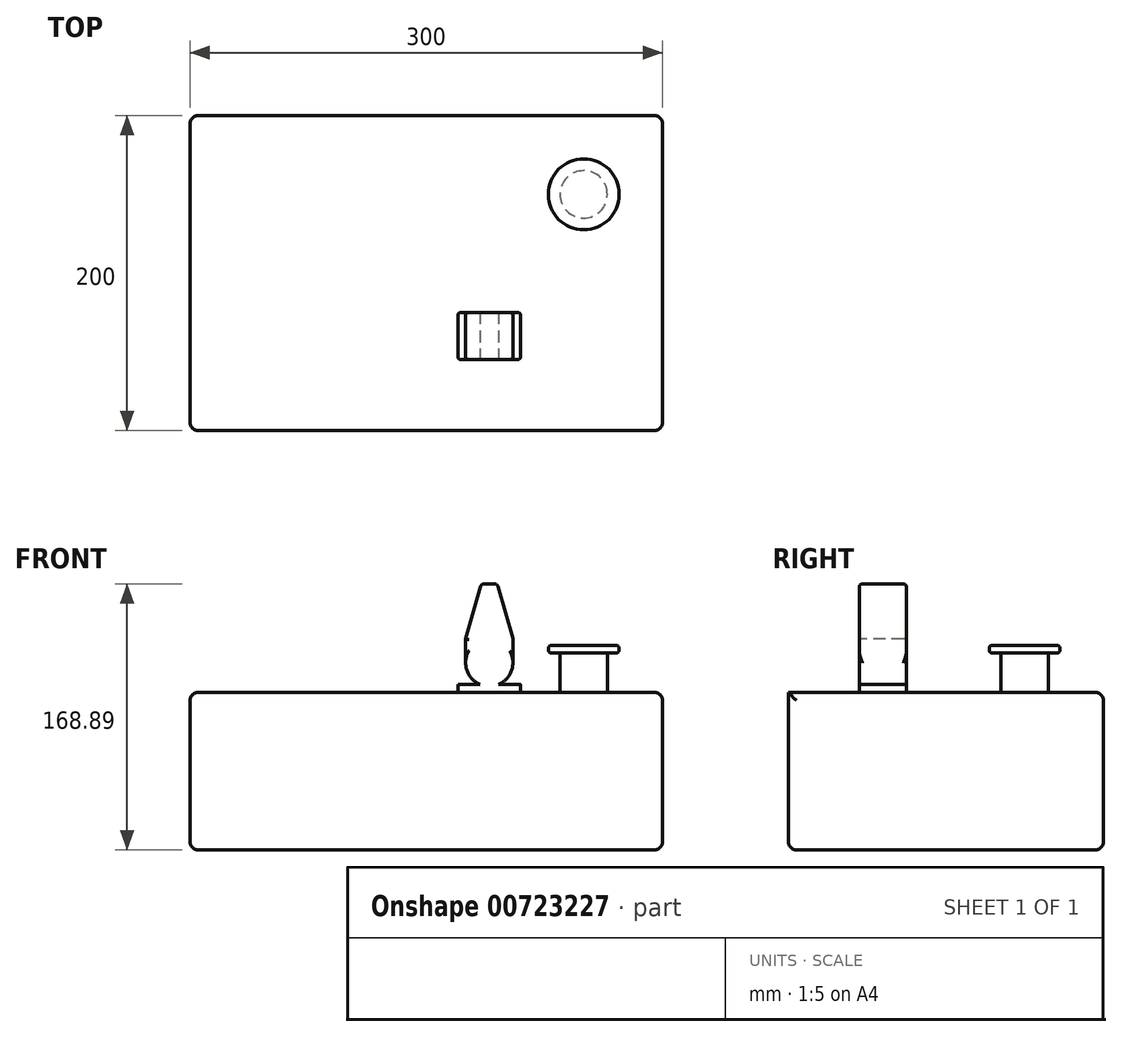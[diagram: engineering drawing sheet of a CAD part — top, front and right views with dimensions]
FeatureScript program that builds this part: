
annotation { "Feature Type Name" : "Feature", "Feature Type Description" : "" }
export const myFeature = defineFeature(function(context is Context, id is Id, definition is map)
    precondition{}
    {
        {
            var Q0;
            Q0=qCreatedBy(makeId("Top.planeOp"),FACE);
            var sketch = newSketch(context, id + "F0", { "sketchPlane" : qUnion([Q0])});
            skLineSegment(sketch, "E0.bottom", {"start": v(-150, 100) * mm, "end": v(150, 100) * mm});
            skLineSegment(sketch, "E0.top", {"start": v(-150, -100) * mm, "end": v(150, -100) * mm});
            skLineSegment(sketch, "E0.left", {"start": v(-150, 100) * mm, "end": v(-150, -100) * mm});
            skLineSegment(sketch, "E0.right", {"start": v(150, 100) * mm, "end": v(150, -100) * mm});
            skSolve(sketch);
        }
        {
            var Q0;
            Q0 = qSketchRegion(id + "F0", true);
            extrude(context, id + "F1", {"entities" : qUnion([Q0]), "depth" : 100 * mm, "offsetDistance" : 25 * mm});
        }
        {
            var Q0;
            Q0=makeQuery(id+"F1.opExtrude","SWEPT_FACE",FACE,{"disambiguationData":[OSD([sQuery(id+"F0.wireOp",EDGE,"E0.top")])]});
            var sketch = newSketch(context, id + "F2", { "sketchPlane" : qUnion([Q0])});
            skLineSegment(sketch, "E1.bottom", {"start": v(20, 100) * mm, "end": v(60, 100) * mm});
            skLineSegment(sketch, "E1.top", {"start": v(20, 105) * mm, "end": v(34.22, 105) * mm});
            skLineSegment(sketch, "E1.left", {"start": v(20, 100) * mm, "end": v(20, 105) * mm});
            skLineSegment(sketch, "E1.right", {"start": v(60, 100) * mm, "end": v(60, 105) * mm});
            skArc(sketch, "E2", {"start": v(25, 118.89) * mm, "mid": v(27.5, 110.54) * mm, "end": v(34.22, 105) * mm});
            skLineSegment(sketch, "E3.top", {"start": v(35, 168.89) * mm, "end": v(45, 168.89) * mm});
            skLineSegment(sketch, "E3.left", {"start": v(25, 118.89) * mm, "end": v(25, 133.89) * mm});
            skLineSegment(sketch, "E3.right", {"start": v(55, 118.89) * mm, "end": v(55, 133.89) * mm});
            skLineSegment(sketch, "E4", {"start": v(35, 168.89) * mm, "end": v(25, 133.89) * mm});
            skLineSegment(sketch, "E5", {"start": v(45, 168.89) * mm, "end": v(55, 133.89) * mm});
            skPoint(sketch, "E6.orphan", {"position": v(25, 168.89) * mm});
            skArc(sketch, "E7.trimOffspring", {"start": v(45.78, 105) * mm, "mid": v(52.5, 110.54) * mm, "end": v(55, 118.89) * mm});
            skLineSegment(sketch, "E8.trimOffspring", {"start": v(45.78, 105) * mm, "end": v(60, 105) * mm});
            skSolve(sketch);
        }
        {
            var Q0;
            Q0 = qSketchRegion(id + "F2", true);
            extrude(context, id + "F3", {"entities" : qUnion([Q0]), "operationType" : NewBodyOperationType.ADD, "oppositeDirection" : true, "depth" : 75 * mm, "offsetDistance" : 25 * mm});
        }
        {
            var Q0;
            Q0=makeQuery(id+"F3.boolean.opBoolean","MERGE",FACE,{"derivedFrom":[makeQuery(id+"F1.opExtrude","SWEPT_FACE",FACE,{"disambiguationData":[OSD([sQuery(id+"F0.wireOp",EDGE,"E0.top")])]}),makeQuery(id+"F3.opExtrude","CAP_FACE",FACE,{"disambiguationData":[OSD([sQuery(id+"F2.wireOp",EDGE,"E1.bottom"),sQuery(id+"F2.wireOp",EDGE,"E1.top"),sQuery(id+"F2.wireOp",EDGE,"E1.left"),sQuery(id+"F2.wireOp",EDGE,"E1.right"),sQuery(id+"F2.wireOp",EDGE,"E2"),sQuery(id+"F2.wireOp",EDGE,"E3.top"),sQuery(id+"F2.wireOp",EDGE,"E3.left"),sQuery(id+"F2.wireOp",EDGE,"E3.right"),sQuery(id+"F2.wireOp",EDGE,"E4"),sQuery(id+"F2.wireOp",EDGE,"E5"),sQuery(id+"F2.wireOp",EDGE,"E7.trimOffspring"),sQuery(id+"F2.wireOp",EDGE,"E8.trimOffspring")])],"isStart":true})]});
            var sketch = newSketch(context, id + "F4", { "sketchPlane" : qUnion([Q0])});
            skLineSegment(sketch, "E9.bottom", {"start": v(9.86, 100) * mm, "end": v(69.53, 100) * mm});
            skLineSegment(sketch, "E9.top", {"start": v(9.86, 173.18) * mm, "end": v(69.53, 173.18) * mm});
            skLineSegment(sketch, "E9.left", {"start": v(9.86, 100) * mm, "end": v(9.86, 173.18) * mm});
            skLineSegment(sketch, "E9.right", {"start": v(69.53, 100) * mm, "end": v(69.53, 173.18) * mm});
            skSolve(sketch);
        }
        {
            var Q0;
            Q0 = qSketchRegion(id + "F4", true);
            extrude(context, id + "F5", {"entities" : qUnion([Q0]), "operationType" : NewBodyOperationType.REMOVE, "oppositeDirection" : true, "depth" : 45 * mm, "offsetDistance" : 25 * mm});
        }
        {
            var Q0;
            Q0=makeQuery(id+"F5.boolean.opBoolean","MERGE",FACE,{"derivedFrom":[makeQuery(id+"F1.opExtrude","CAP_FACE",FACE,{"disambiguationData":[OSD([sQuery(id+"F0.wireOp",EDGE,"E0.bottom"),sQuery(id+"F0.wireOp",EDGE,"E0.top"),sQuery(id+"F0.wireOp",EDGE,"E0.left"),sQuery(id+"F0.wireOp",EDGE,"E0.right")])],"isStart":false}),makeQuery(id+"F5.opExtrude","SWEPT_FACE",FACE,{"disambiguationData":[OSD([sQuery(id+"F4.wireOp",EDGE,"E9.bottom")])]})]});
            var sketch = newSketch(context, id + "F6", { "sketchPlane" : qUnion([Q0])});
            skCircle(sketch, "E10", {"center": v(100, 50) * mm, "radius": 15 * mm});
            skSolve(sketch);
        }
        {
            var Q0;
            Q0 = qSketchRegion(id + "F6", true);
            extrude(context, id + "F7", {"entities" : qUnion([Q0]), "operationType" : NewBodyOperationType.ADD, "depth" : 25 * mm, "offsetDistance" : 25 * mm});
        }
        {
            var Q0;
            Q0=makeQuery(id+"F7.opExtrude","CAP_FACE",FACE,{"disambiguationData":[OSD([sQuery(id+"F6.wireOp",EDGE,"E10")])],"isStart":false});
            var sketch = newSketch(context, id + "F8", { "sketchPlane" : qUnion([Q0])});
            skCircle(sketch, "E11", {"center": v(100, 50) * mm, "radius": 22.5 * mm});
            skSolve(sketch);
        }
        {
            var Q0;
            Q0 = qSketchRegion(id + "F8", true);
            extrude(context, id + "F9", {"entities" : qUnion([Q0]), "operationType" : NewBodyOperationType.ADD, "depth" : 5 * mm, "offsetDistance" : 25 * mm});
        }
        {
            var Q0;
            Q0=makeQuery(id+"F5.boolean.opBoolean","INTERSECT",EDGE,{"derivedFrom":[makeQuery(id+"F3.opExtrude","SWEPT_FACE",FACE,{"disambiguationData":[OSD([sQuery(id+"F2.wireOp",EDGE,"E4")])]}),makeQuery(id+"F5.opExtrude","CAP_FACE",FACE,{"disambiguationData":[OSD([sQuery(id+"F4.wireOp",EDGE,"E9.bottom"),sQuery(id+"F4.wireOp",EDGE,"E9.top"),sQuery(id+"F4.wireOp",EDGE,"E9.left"),sQuery(id+"F4.wireOp",EDGE,"E9.right")])],"isStart":false})]});
            var Q1;
            Q1=makeQuery(id+"F5.boolean.opBoolean","INTERSECT",EDGE,{"derivedFrom":[makeQuery(id+"F3.opExtrude","SWEPT_FACE",FACE,{"disambiguationData":[OSD([sQuery(id+"F2.wireOp",EDGE,"E5")])]}),makeQuery(id+"F5.opExtrude","CAP_FACE",FACE,{"disambiguationData":[OSD([sQuery(id+"F4.wireOp",EDGE,"E9.bottom"),sQuery(id+"F4.wireOp",EDGE,"E9.top"),sQuery(id+"F4.wireOp",EDGE,"E9.left"),sQuery(id+"F4.wireOp",EDGE,"E9.right")])],"isStart":false})]});
            var Q2;
            Q2=makeQuery(id+"F3.opExtrude","SWEPT_EDGE",EDGE,{"disambiguationData":[OSD([sQuery(id+"F2.wireOp",EDGE,"E3.right"),sQuery(id+"F2.wireOp",EDGE,"E5")])]});
            var Q3;
            Q3=makeQuery(id+"F3.opExtrude","CAP_EDGE",EDGE,{"disambiguationData":[OSD([sQuery(id+"F2.wireOp",EDGE,"E4")])],"isStart":false});
            var Q4;
            Q4=makeQuery(id+"F3.opExtrude","CAP_EDGE",EDGE,{"disambiguationData":[OSD([sQuery(id+"F2.wireOp",EDGE,"E3.left")])],"isStart":false});
            var Q5;
            Q5=makeQuery(id+"F3.opExtrude","CAP_EDGE",EDGE,{"disambiguationData":[OSD([sQuery(id+"F2.wireOp",EDGE,"E3.right")])],"isStart":false});
            var Q6;
            Q6=makeQuery(id+"F5.boolean.opBoolean","INTERSECT",EDGE,{"derivedFrom":[makeQuery(id+"F3.opExtrude","SWEPT_FACE",FACE,{"disambiguationData":[OSD([sQuery(id+"F2.wireOp",EDGE,"E3.right")])]}),makeQuery(id+"F5.opExtrude","CAP_FACE",FACE,{"disambiguationData":[OSD([sQuery(id+"F4.wireOp",EDGE,"E9.bottom"),sQuery(id+"F4.wireOp",EDGE,"E9.top"),sQuery(id+"F4.wireOp",EDGE,"E9.left"),sQuery(id+"F4.wireOp",EDGE,"E9.right")])],"isStart":false})]});
            var Q7;
            Q7=makeQuery(id+"F5.boolean.opBoolean","INTERSECT",EDGE,{"derivedFrom":[makeQuery(id+"F3.opExtrude","SWEPT_FACE",FACE,{"disambiguationData":[OSD([sQuery(id+"F2.wireOp",EDGE,"E3.left")])]}),makeQuery(id+"F5.opExtrude","CAP_FACE",FACE,{"disambiguationData":[OSD([sQuery(id+"F4.wireOp",EDGE,"E9.bottom"),sQuery(id+"F4.wireOp",EDGE,"E9.top"),sQuery(id+"F4.wireOp",EDGE,"E9.left"),sQuery(id+"F4.wireOp",EDGE,"E9.right")])],"isStart":false})]});
            var Q8;
            Q8=makeQuery(id+"F3.opExtrude","CAP_EDGE",EDGE,{"disambiguationData":[OSD([sQuery(id+"F2.wireOp",EDGE,"E1.left")])],"isStart":false});
            var Q9;
            Q9=makeQuery(id+"F3.opExtrude","CAP_EDGE",EDGE,{"disambiguationData":[OSD([sQuery(id+"F2.wireOp",EDGE,"E1.right")])],"isStart":false});
            var Q10;
            Q10=makeQuery(id+"F5.boolean.opBoolean","INTERSECT",EDGE,{"derivedFrom":[makeQuery(id+"F3.opExtrude","SWEPT_FACE",FACE,{"disambiguationData":[OSD([sQuery(id+"F2.wireOp",EDGE,"E1.left")])]}),makeQuery(id+"F5.opExtrude","CAP_FACE",FACE,{"disambiguationData":[OSD([sQuery(id+"F4.wireOp",EDGE,"E9.bottom"),sQuery(id+"F4.wireOp",EDGE,"E9.top"),sQuery(id+"F4.wireOp",EDGE,"E9.left"),sQuery(id+"F4.wireOp",EDGE,"E9.right")])],"isStart":false})]});
            var Q11;
            Q11=makeQuery(id+"F5.boolean.opBoolean","INTERSECT",EDGE,{"derivedFrom":[makeQuery(id+"F3.opExtrude","SWEPT_FACE",FACE,{"disambiguationData":[OSD([sQuery(id+"F2.wireOp",EDGE,"E1.right")])]}),makeQuery(id+"F5.opExtrude","CAP_FACE",FACE,{"disambiguationData":[OSD([sQuery(id+"F4.wireOp",EDGE,"E9.bottom"),sQuery(id+"F4.wireOp",EDGE,"E9.top"),sQuery(id+"F4.wireOp",EDGE,"E9.left"),sQuery(id+"F4.wireOp",EDGE,"E9.right")])],"isStart":false})]});
            var Q12;
            Q12=makeQuery(id+"F9.opExtrude","CAP_EDGE",EDGE,{"disambiguationData":[OSD([sQuery(id+"F8.wireOp",EDGE,"E11")])],"isStart":false});
            var Q13;
            Q13=makeQuery(id+"F9.opExtrude","CAP_EDGE",EDGE,{"disambiguationData":[OSD([sQuery(id+"F8.wireOp",EDGE,"E11")])],"isStart":true});
            var Q14;
            Q14=makeQuery(id+"F3.opExtrude","CAP_EDGE",EDGE,{"disambiguationData":[OSD([sQuery(id+"F2.wireOp",EDGE,"E5")])],"isStart":false});
            var Q15;
            Q15=makeQuery(id+"F3.opExtrude","SWEPT_EDGE",EDGE,{"disambiguationData":[OSD([sQuery(id+"F2.wireOp",EDGE,"E3.top"),sQuery(id+"F2.wireOp",EDGE,"E5")])]});
            var Q16;
            Q16=makeQuery(id+"F3.opExtrude","SWEPT_EDGE",EDGE,{"disambiguationData":[OSD([sQuery(id+"F2.wireOp",EDGE,"E3.top"),sQuery(id+"F2.wireOp",EDGE,"E4")])]});
            var Q17;
            Q17=makeQuery(id+"F3.opExtrude","CAP_EDGE",EDGE,{"disambiguationData":[OSD([sQuery(id+"F2.wireOp",EDGE,"E3.top")])],"isStart":false});
            var Q18;
            Q18=makeQuery(id+"F5.boolean.opBoolean","INTERSECT",EDGE,{"derivedFrom":[makeQuery(id+"F3.opExtrude","SWEPT_FACE",FACE,{"disambiguationData":[OSD([sQuery(id+"F2.wireOp",EDGE,"E3.top")])]}),makeQuery(id+"F5.opExtrude","CAP_FACE",FACE,{"disambiguationData":[OSD([sQuery(id+"F4.wireOp",EDGE,"E9.bottom"),sQuery(id+"F4.wireOp",EDGE,"E9.top"),sQuery(id+"F4.wireOp",EDGE,"E9.left"),sQuery(id+"F4.wireOp",EDGE,"E9.right")])],"isStart":false})]});
            fillet(context, id + "F10", {"entities" : qUnion([Q0, Q1, Q2, Q3, Q4, Q5, Q6, Q7, Q8, Q9, Q10, Q11, Q12, Q13, Q14, Q15, Q16, Q17, Q18]), "radius" : 2 * mm, "tangentPropagation" : true, "allowEdgeOverflow" : false});
        }
        {
            var Q0;
            {var subQ3=sQuery(id+"F0.wireOp",EDGE,"E0.right");var subQ4=sQuery(id+"F0.wireOp",EDGE,"E0.top");var subQ6=sQuery(id+"F0.wireOp",EDGE,"E0.left");var subQ8=makeQuery(id+"F1.opExtrude","CAP_EDGE",EDGE,{"disambiguationData":[OSD([subQ4])],"isStart":false});Q0=makeQuery(id+"F5.boolean.opBoolean","MERGE",EDGE,{"derivedFrom":[makeQuery(id+"F3.boolean.opBoolean","SPLIT",EDGE,{"disambiguationData":[TD([makeQuery(id+"F1.opExtrude","SWEPT_FACE",FACE,{"disambiguationData":[OSD([subQ6])]})])],"derivedFrom":subQ8}),makeQuery(id+"F3.boolean.opBoolean","SPLIT",EDGE,{"disambiguationData":[TD([makeQuery(id+"F1.opExtrude","SWEPT_FACE",FACE,{"disambiguationData":[OSD([subQ3])]})])],"derivedFrom":subQ8}),makeQuery(id+"F5.opExtrude","CAP_EDGE",EDGE,{"disambiguationData":[OSD([sQuery(id+"F4.wireOp",EDGE,"E9.bottom")])],"isStart":true})]});}
            var Q1;
            Q1=makeQuery(id+"F1.opExtrude","CAP_EDGE",EDGE,{"disambiguationData":[OSD([sQuery(id+"F0.wireOp",EDGE,"E0.left")])],"isStart":false});
            var Q2;
            Q2=makeQuery(id+"F1.opExtrude","SWEPT_EDGE",EDGE,{"disambiguationData":[OSD([sQuery(id+"F0.wireOp",EDGE,"E0.top"),sQuery(id+"F0.wireOp",EDGE,"E0.left")])]});
            var Q3;
            Q3=makeQuery(id+"F1.opExtrude","CAP_EDGE",EDGE,{"disambiguationData":[OSD([sQuery(id+"F0.wireOp",EDGE,"E0.top")])],"isStart":true});
            var Q4;
            Q4=makeQuery(id+"F1.opExtrude","CAP_EDGE",EDGE,{"disambiguationData":[OSD([sQuery(id+"F0.wireOp",EDGE,"E0.left")])],"isStart":true});
            var Q5;
            Q5=makeQuery(id+"F1.opExtrude","SWEPT_EDGE",EDGE,{"disambiguationData":[OSD([sQuery(id+"F0.wireOp",EDGE,"E0.top"),sQuery(id+"F0.wireOp",EDGE,"E0.right")])]});
            var Q6;
            Q6=makeQuery(id+"F1.opExtrude","CAP_EDGE",EDGE,{"disambiguationData":[OSD([sQuery(id+"F0.wireOp",EDGE,"E0.right")])],"isStart":true});
            var Q7;
            Q7=makeQuery(id+"F1.opExtrude","CAP_EDGE",EDGE,{"disambiguationData":[OSD([sQuery(id+"F0.wireOp",EDGE,"E0.bottom")])],"isStart":true});
            var Q8;
            Q8=makeQuery(id+"F1.opExtrude","CAP_EDGE",EDGE,{"disambiguationData":[OSD([sQuery(id+"F0.wireOp",EDGE,"E0.bottom")])],"isStart":false});
            var Q9;
            Q9=makeQuery(id+"F1.opExtrude","CAP_EDGE",EDGE,{"disambiguationData":[OSD([sQuery(id+"F0.wireOp",EDGE,"E0.right")])],"isStart":false});
            var Q10;
            Q10=makeQuery(id+"F1.opExtrude","SWEPT_EDGE",EDGE,{"disambiguationData":[OSD([sQuery(id+"F0.wireOp",EDGE,"E0.bottom"),sQuery(id+"F0.wireOp",EDGE,"E0.left")])]});
            var Q11;
            Q11=makeQuery(id+"F1.opExtrude","SWEPT_EDGE",EDGE,{"disambiguationData":[OSD([sQuery(id+"F0.wireOp",EDGE,"E0.bottom"),sQuery(id+"F0.wireOp",EDGE,"E0.right")])]});
            fillet(context, id + "F11", {"entities" : qUnion([Q0, Q1, Q2, Q3, Q4, Q5, Q6, Q7, Q8, Q9, Q10, Q11]), "radius" : 5 * mm, "tangentPropagation" : true, "allowEdgeOverflow" : false});
        }
    });
